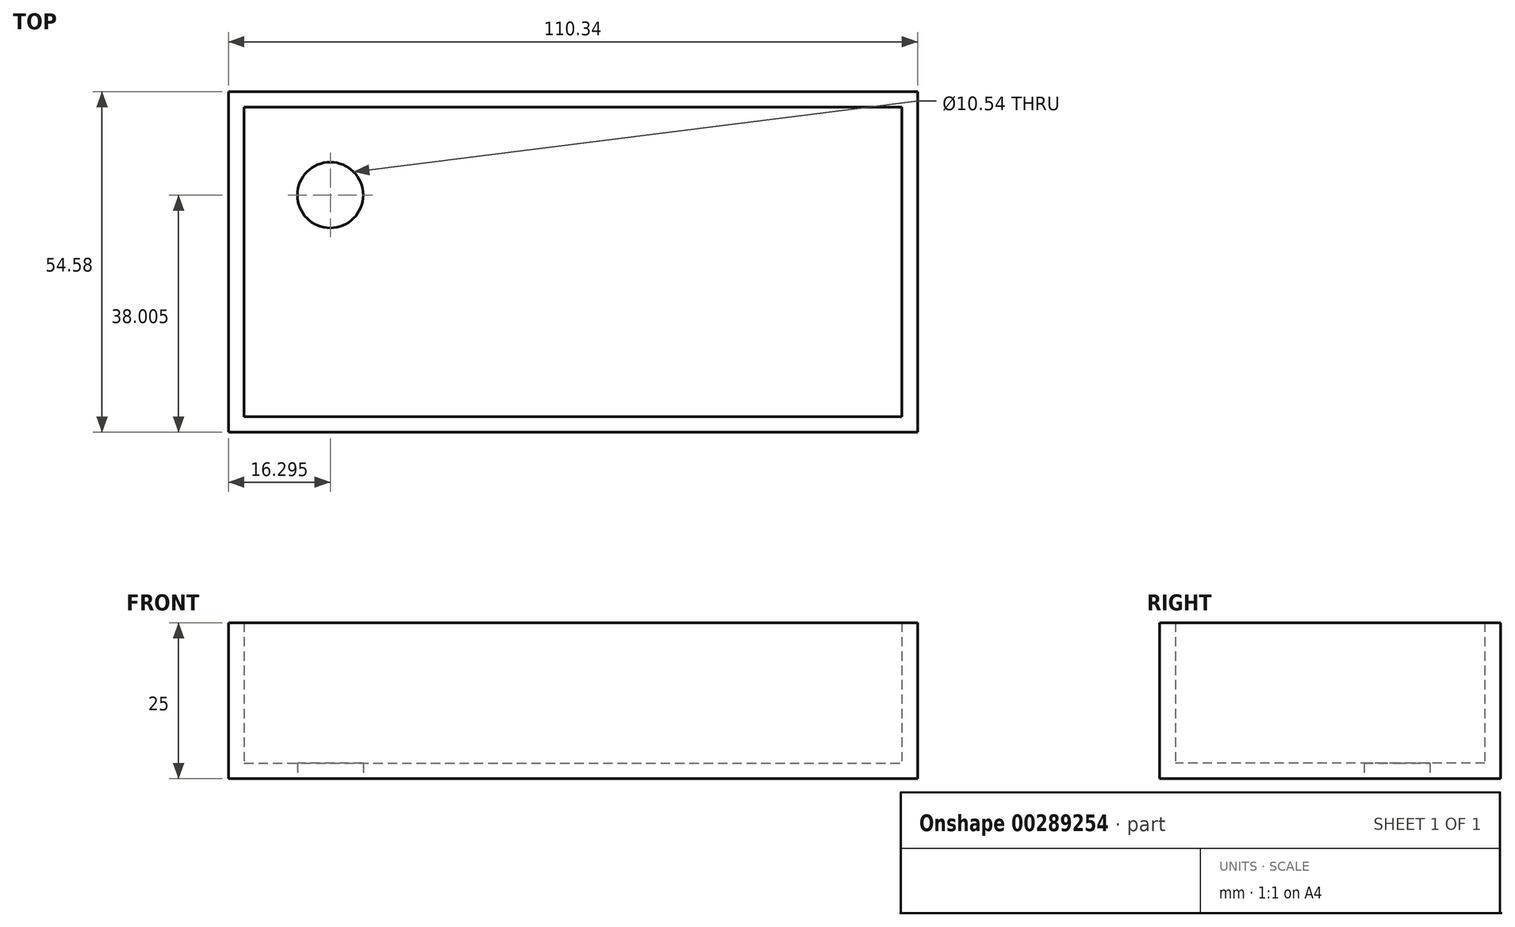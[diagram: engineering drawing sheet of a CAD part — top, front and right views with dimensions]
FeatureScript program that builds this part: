
annotation { "Feature Type Name" : "Feature", "Feature Type Description" : "" }
export const myFeature = defineFeature(function(context is Context, id is Id, definition is map)
    precondition{}
    {
        {
            var Q0;
            Q0=qCreatedBy(makeId("Top.planeOp"),FACE);
            var sketch = newSketch(context, id + "F0", { "sketchPlane" : qUnion([Q0])});
            skLineSegment(sketch, "E0.bottom", {"start": v(-55.17, 27.3) * mm, "end": v(55.17, 27.3) * mm});
            skLineSegment(sketch, "E0.top", {"start": v(-55.17, -27.3) * mm, "end": v(55.17, -27.3) * mm});
            skLineSegment(sketch, "E0.left", {"start": v(-55.17, 27.3) * mm, "end": v(-55.17, -27.3) * mm});
            skLineSegment(sketch, "E0.right", {"start": v(55.17, 27.3) * mm, "end": v(55.17, -27.3) * mm});
            skPoint(sketch, "E0.middle", {"position": v(0, 0) * mm});
            skSolve(sketch);
        }
        {
            var Q0;
            Q0 = qSketchRegion(id + "F0", true);
            extrude(context, id + "F1", {"entities" : qUnion([Q0]), "depth" : 25 * mm});
        }
        {
            var Q0;
            Q0=makeQuery(id+"F1.opExtrude","CAP_FACE",FACE,{"disambiguationData":[OSD([sQuery(id+"F0.wireOp",EDGE,"E0.bottom"),sQuery(id+"F0.wireOp",EDGE,"E0.top"),sQuery(id+"F0.wireOp",EDGE,"E0.left"),sQuery(id+"F0.wireOp",EDGE,"E0.right")])],"isStart":false});
            shell(context, id + "F2", {"entities" : qUnion([Q0]), "thickness" : 2.5 * mm});
        }
        {
            var Q0;
            Q0=qCreatedBy(makeId("Top.planeOp"),FACE);
            var sketch = newSketch(context, id + "F3", { "sketchPlane" : qUnion([Q0])});
            skCircle(sketch, "E1", {"center": v(-38.87, 10.71) * mm, "radius": 5.27 * mm});
            skSolve(sketch);
        }
        {
            var Q0;
            Q0 = qSketchRegion(id + "F3", true);
            extrude(context, id + "F4", {"entities" : qUnion([Q0]), "operationType" : NewBodyOperationType.REMOVE, "endBound" : BoundingType.THROUGH_ALL, "depth" : 25 * mm});
        }
    });
